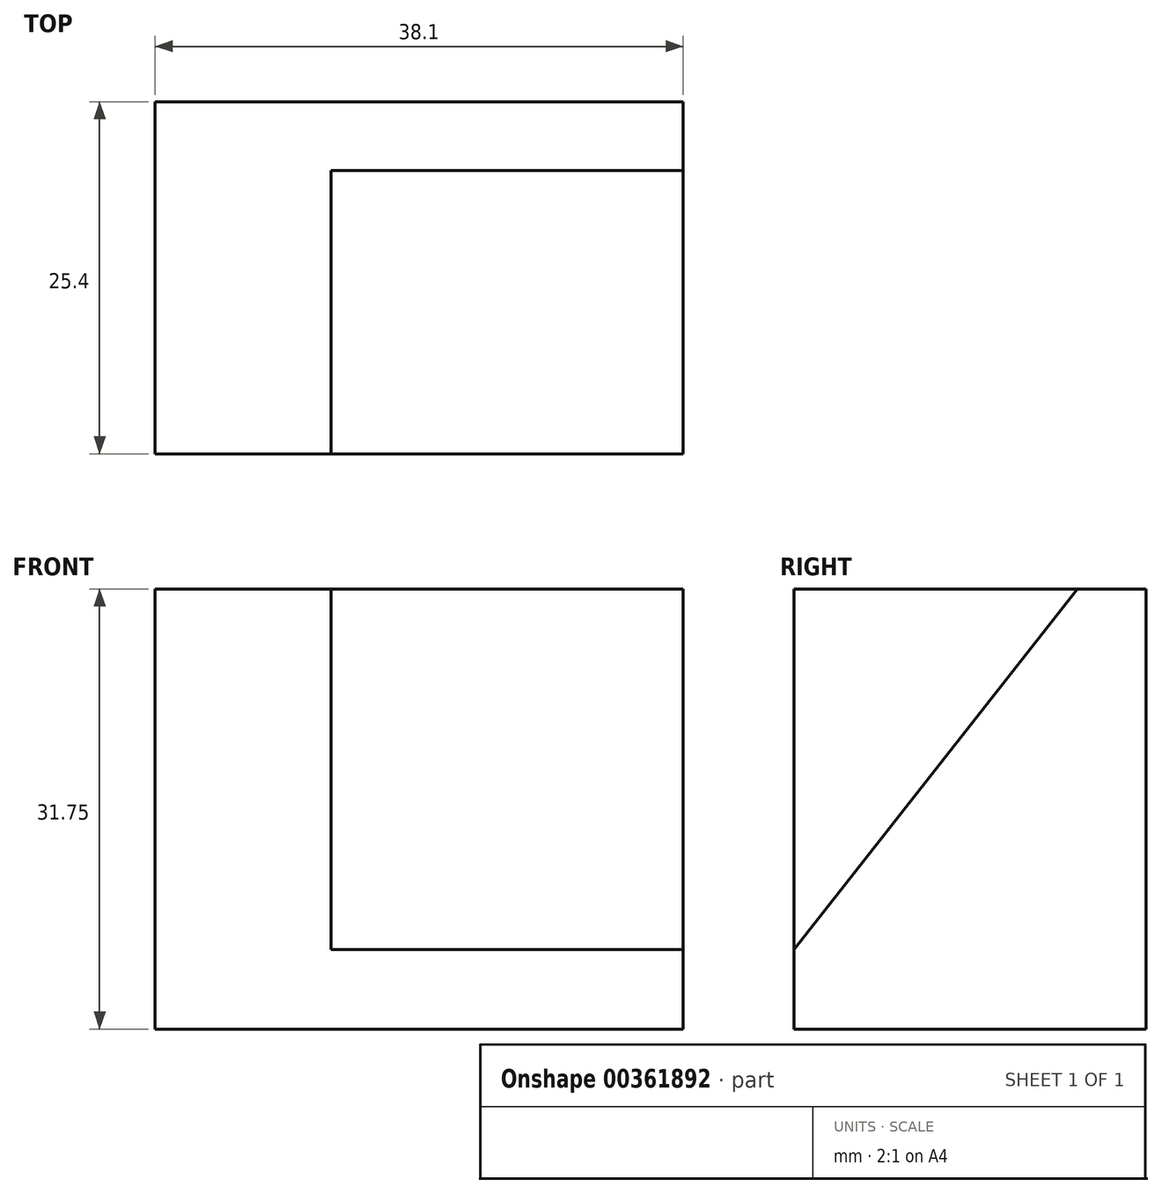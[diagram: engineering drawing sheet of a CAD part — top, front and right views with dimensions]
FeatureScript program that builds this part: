
annotation { "Feature Type Name" : "Feature", "Feature Type Description" : "" }
export const myFeature = defineFeature(function(context is Context, id is Id, definition is map)
    precondition{}
    {
        {
            var Q0;
            Q0=qCreatedBy(makeId("Front.planeOp"),FACE);
            var sketch = newSketch(context, id + "F0", { "sketchPlane" : qUnion([Q0])});
            skLineSegment(sketch, "E0", {"start": v(0, 0) * mm, "end": v(38.1, 0) * mm});
            skLineSegment(sketch, "E1", {"start": v(38.1, 0) * mm, "end": v(38.1, 31.75) * mm});
            skLineSegment(sketch, "E2", {"start": v(38.1, 31.75) * mm, "end": v(0, 31.75) * mm});
            skLineSegment(sketch, "E3", {"start": v(0, 31.75) * mm, "end": v(0, 0) * mm});
            skSolve(sketch);
        }
        {
            var Q0;
            Q0=makeQuery(id+"F0.imprint","IMPRINT",FACE,{"disambiguationData":[TD([[makeQuery(id+"F0.imprint","IMPRINT",EDGE,{"derivedFrom":sQuery(id+"F0.wireOp",EDGE,"E0")}),1.0]])]});
            extrude(context, id + "F1", {"entities" : qUnion([Q0]), "depth" : 25.4 * mm});
        }
        {
            var Q0;
            Q0=makeQuery(id+"F1.opExtrude","SWEPT_FACE",FACE,{"disambiguationData":[OSD([sQuery(id+"F0.wireOp",EDGE,"E1")])]});
            var sketch = newSketch(context, id + "F2", { "sketchPlane" : qUnion([Q0])});
            skLineSegment(sketch, "E4", {"start": v(-4.95, 31.75) * mm, "end": v(-25.4, 5.73) * mm});
            skSolve(sketch);
        }
        {
            var Q0;
            {var subQ0=sQuery(id+"F2.wireOp",EDGE,"E4");Q0=makeQuery(id+"F2.imprint","IMPRINT",FACE,{"disambiguationData":[TD([[makeQuery(id+"F2.imprint","IMPRINT",EDGE,{"derivedFrom":subQ0}),-1.0]])]});}
            extrude(context, id + "F3", {"entities" : qUnion([Q0]), "operationType" : NewBodyOperationType.REMOVE, "oppositeDirection" : true, "depth" : 25.4 * mm});
        }
    });
